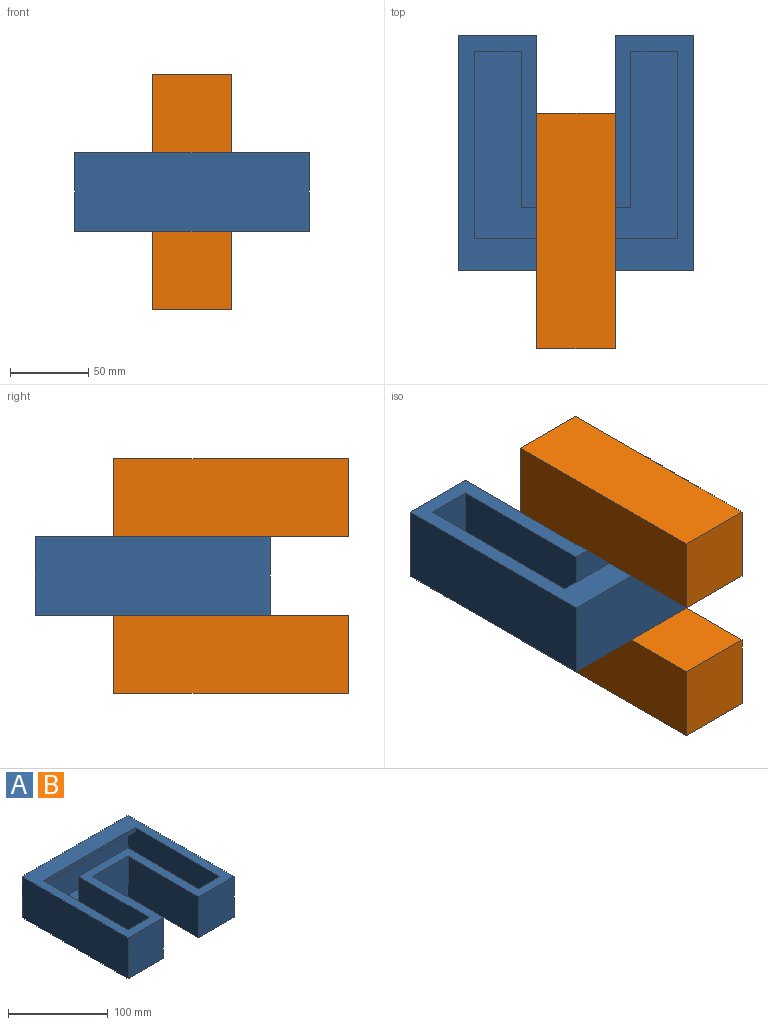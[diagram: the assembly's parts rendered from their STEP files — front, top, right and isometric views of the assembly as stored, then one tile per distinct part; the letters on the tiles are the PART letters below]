
ASSEMBLY  parts=2 mates=1
PART A: 21 faces, bbox 150x150x50 mm
  f0: plane 130x40mm, normal (0,-1,0), area 5200mm2, adj f1,f10,f18,f19
  f1: plane 130x45mm, normal (-1,0,0), area 5800mm2, adj f0,f11,f17,f18,f19,f20
  f2: plane 150x150mm, normal (0,0,-1), area 17500mm2, adj f3,f4,f5,f6,f7,f8,f9,f16
  f3: plane 150x50mm, normal (-1,0,0), area 7500mm2, adj f2,f4,f16,f17
  f4: plane 50x50mm, normal (0,-1,0), area 2500mm2, adj f2,f3,f5,f17
  f5: plane 100x50mm, normal (1,0,0), area 5000mm2, adj f2,f4,f6,f17
  f6: plane 50x50mm, normal (0,-1,0), area 2500mm2, adj f2,f5,f7,f17
  f7: plane 100x50mm, normal (-1,0,0), area 5000mm2, adj f2,f6,f8,f17
  f8: plane 50x50mm, normal (0,-1,0), area 2500mm2, adj f2,f7,f9,f17
  f9: plane 150x50mm, normal (1,0,0), area 7500mm2, adj f2,f8,f16,f17
  f10: plane 130x45mm, normal (1,0,0), area 5800mm2, adj f0,f15,f17,f18,f19,f20
  f11: plane 45x30mm, normal (0,1,0), area 1350mm2, adj f1,f12,f17,f18
  f12: plane 100x45mm, normal (1,0,0), area 4500mm2, adj f11,f13,f17,f18
  f13: plane 70x45mm, normal (0,1,0), area 3150mm2, adj f12,f14,f17,f18
  f14: plane 100x45mm, normal (-1,0,0), area 4500mm2, adj f13,f15,f17,f18
  f15: plane 45x30mm, normal (0,1,0), area 1350mm2, adj f10,f14,f17,f18
  f16: plane 150x50mm, normal (0,1,0), area 7500mm2, adj f2,f3,f9,f17
  f17: plane 150x150mm, normal (0,0,1), area 8900mm2, adj f1,f3,f4,f5,f6,f7,f8,f9
  f18: plane 130x130mm, normal (0,0,1), area 9900mm2, adj f0,f1,f10,f11,f12,f13,f14,f15
  f19: plane 130x10mm, normal (0,0,-1), area 1300mm2, adj f0,f1,f10,f20
  f20: plane 130x5mm, normal (0,-1,0), area 650mm2, adj f1,f10,f17,f19
PART B: same geometry as A
PLACE A rot(axis=(0,0,-1),180deg) t=(-128.18,6.09,67.7)mm
PLACE B rot(axis=(0,1,0),90deg) t=(-78.18,-193.91,17.7)mm
MATE fastened B.f6 <-> A.f6  axis (0,-1,0) through (-53.18,-93.91,92.7)mm
